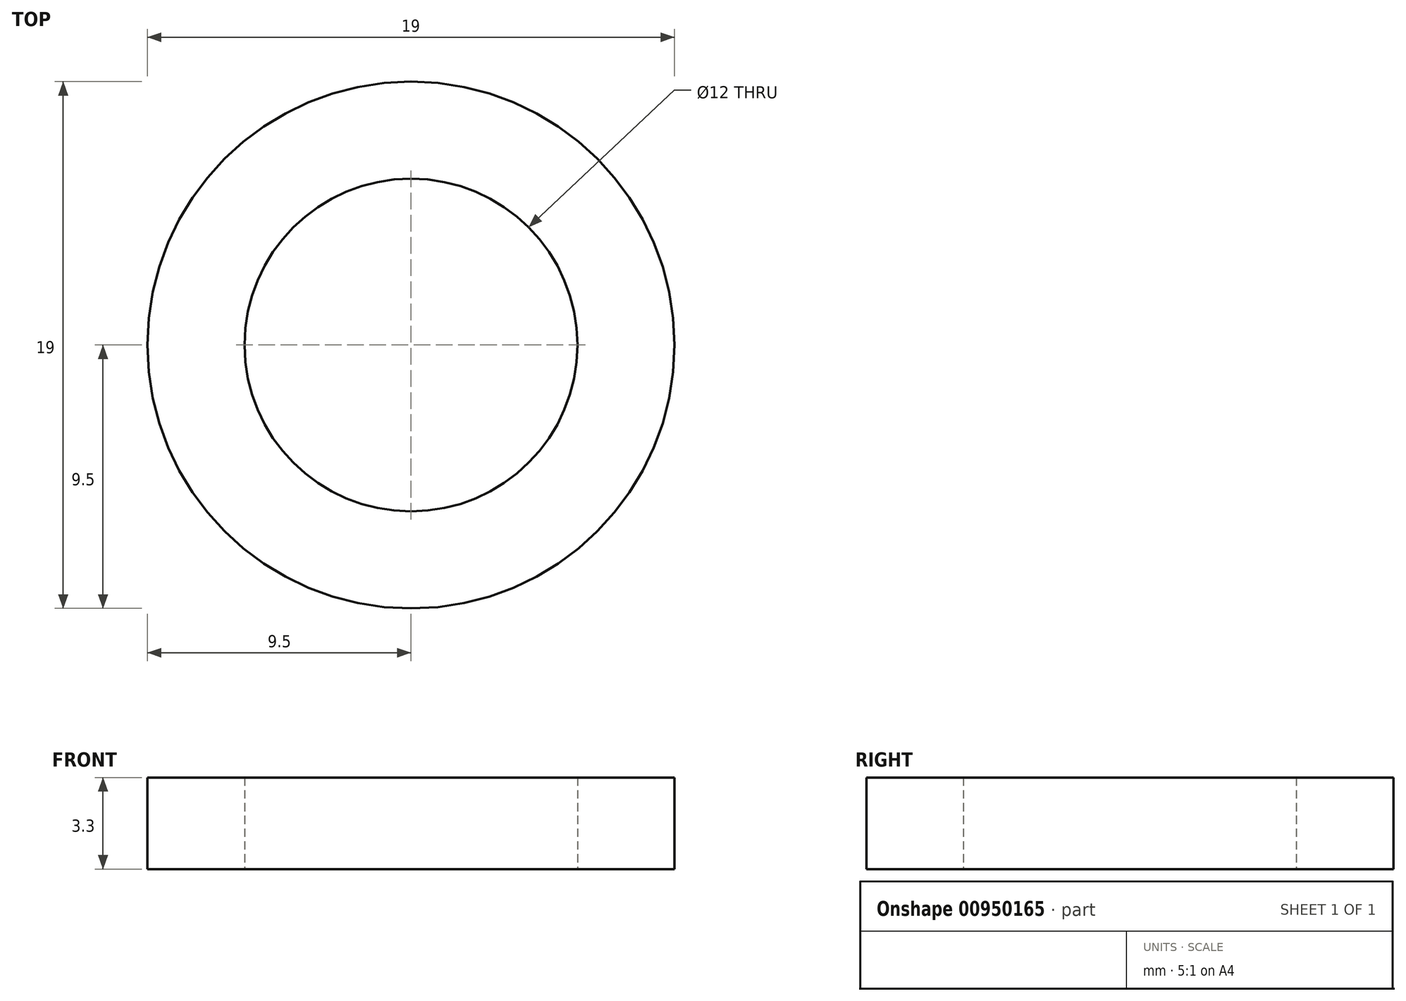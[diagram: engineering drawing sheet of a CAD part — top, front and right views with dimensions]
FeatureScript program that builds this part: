
annotation { "Feature Type Name" : "Feature", "Feature Type Description" : "" }
export const myFeature = defineFeature(function(context is Context, id is Id, definition is map)
    precondition{}
    {
        {
            var Q0;
            Q0=qCreatedBy(makeId("Top.planeOp"),FACE);
            var sketch = newSketch(context, id + "F0", { "sketchPlane" : qUnion([Q0])});
            skCircle(sketch, "E0", {"center": v(0, 0) * mm, "radius": 9.5 * mm});
            skCircle(sketch, "E1", {"center": v(0, 0) * mm, "radius": 6 * mm});
            skSolve(sketch);
        }
        {
            var Q0;
            Q0 = qSketchRegion(id + "F0", true);
            extrude(context, id + "F1", {"entities" : qUnion([Q0]), "depth" : 3.3 * mm, "offsetDistance" : 25.4 * mm});
        }
    });
